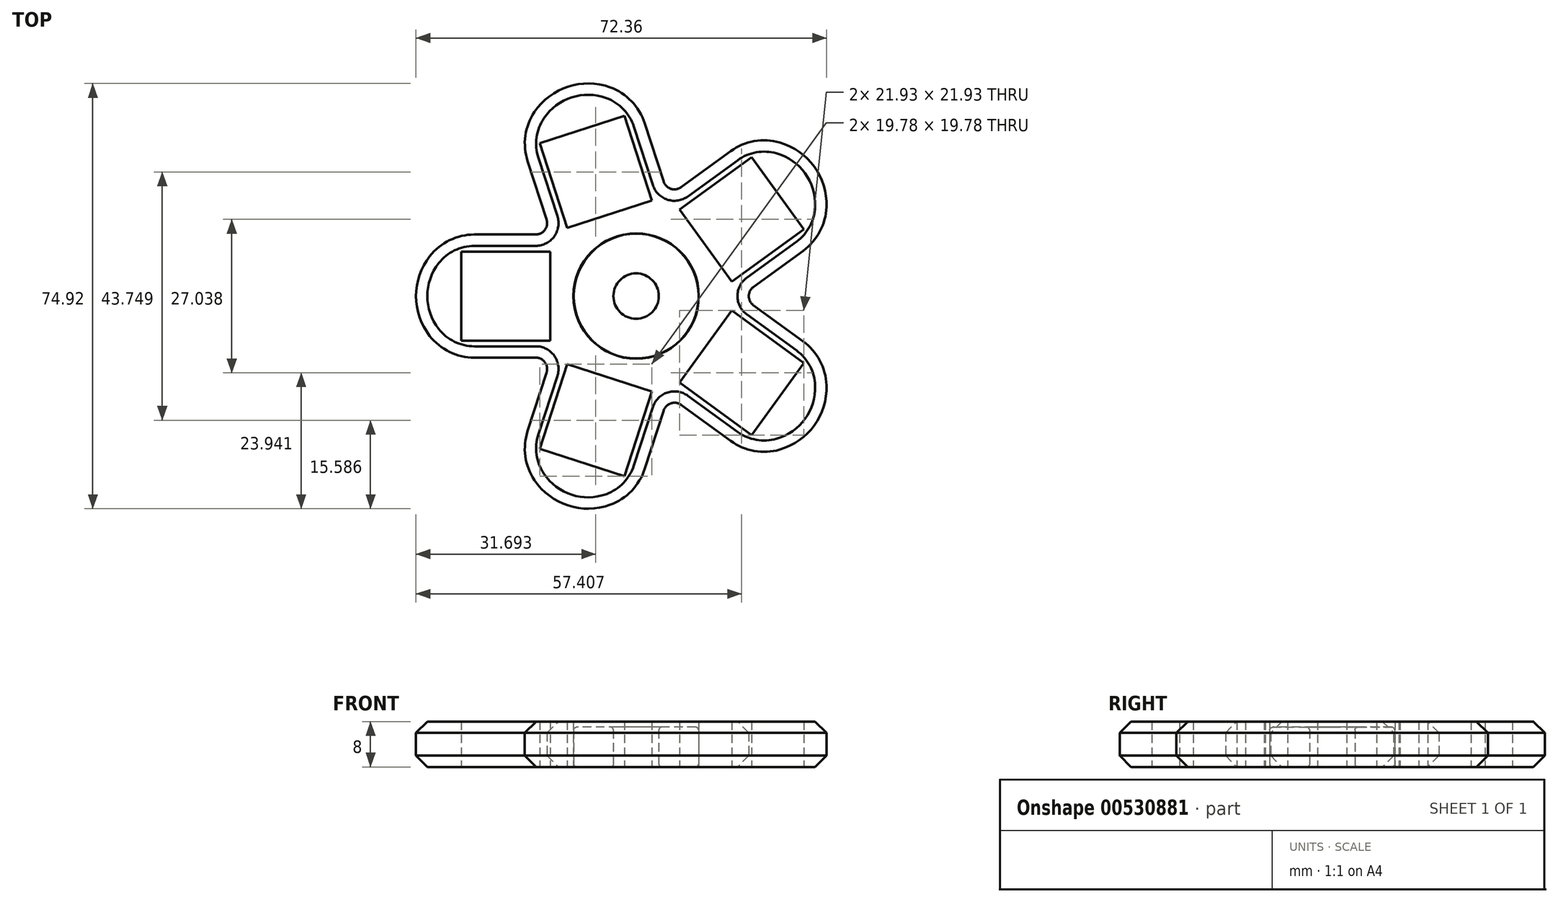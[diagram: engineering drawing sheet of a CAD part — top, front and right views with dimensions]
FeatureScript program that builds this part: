
annotation { "Feature Type Name" : "Feature", "Feature Type Description" : "" }
export const myFeature = defineFeature(function(context is Context, id is Id, definition is map)
    precondition{}
    {
        {
            var Q0;
            Q0=qCreatedBy(makeId("Top.planeOp"),FACE);
            var sketch = newSketch(context, id + "F0", { "sketchPlane" : qUnion([Q0])});
            skCircle(sketch, "E0", {"center": v(0, 0) * mm, "radius": 11 * mm});
            skCircle(sketch, "E1", {"center": v(0, 0) * mm, "radius": 4 * mm});
            skSolve(sketch);
        }
        {
            var Q0;
            Q0=makeQuery(id+"F0.imprint","IMPRINT",FACE,{"disambiguationData":[TD([[makeQuery(id+"F0.imprint","IMPRINT",EDGE,{"derivedFrom":sQuery(id+"F0.wireOp",EDGE,"E0")}),1.0]])]});
            extrude(context, id + "F1", {"entities" : qUnion([Q0]), "depth" : 7 * mm, "offsetDistance" : 25 * mm});
        }
        {
            var Q0;
            Q0=makeQuery(id+"F1.opExtrude","CAP_FACE",FACE,{"disambiguationData":[OSD([sQuery(id+"F0.wireOp",EDGE,"E0"),sQuery(id+"F0.wireOp",EDGE,"E1")])],"isStart":true});
            var sketch = newSketch(context, id + "F2", { "sketchPlane" : qUnion([Q0])});
            skCircle(sketch, "E2.0", {"center": v(0, 0) * mm, "radius": 11.05 * mm});
            skCircle(sketch, "E3.0", {"center": v(0, 0) * mm, "radius": 15.05 * mm});
            skLineSegment(sketch, "E4", {"start": v(0, 0) * mm, "end": v(-23, 0) * mm, "construction": true});
            skLineSegment(sketch, "E5.bottom", {"start": v(-30.85, -7.85) * mm, "end": v(-15.15, -7.85) * mm});
            skLineSegment(sketch, "E5.top", {"start": v(-30.85, 7.85) * mm, "end": v(-15.15, 7.85) * mm});
            skLineSegment(sketch, "E5.left", {"start": v(-30.85, -7.85) * mm, "end": v(-30.85, 7.85) * mm});
            skLineSegment(sketch, "E5.right", {"start": v(-15.15, -7.85) * mm, "end": v(-15.15, 7.85) * mm});
            skPoint(sketch, "E5.middle", {"position": v(-23, 0) * mm});
            skCircle(sketch, "E6", {"center": v(0, 0) * mm, "radius": 50 * mm, "construction": true});
            skLineSegment(sketch, "E7", {"start": v(-23, 0) * mm, "end": v(-38.8, 0) * mm, "construction": true});
            skLineSegment(sketch, "E8", {"start": v(-30.85, 7.85) * mm, "end": v(-30.85, 10.85) * mm, "construction": true});
            skLineSegment(sketch, "E9.0", {"start": v(-23, 10.85) * mm, "end": v(-30.85, 10.85) * mm});
            skLineSegment(sketch, "E9.1", {"start": v(0, 10.85) * mm, "end": v(-2.1, 10.85) * mm, "construction": true});
            skLineSegment(sketch, "E10.trimOffspring", {"start": v(-10.43, 10.85) * mm, "end": v(-23, 10.85) * mm});
            skLineSegment(sketch, "E11.MirrorCS", {"start": v(-10.43, -10.85) * mm, "end": v(-23, -10.85) * mm});
            skLineSegment(sketch, "E12.MirrorCS", {"start": v(-23, -10.85) * mm, "end": v(-30.85, -10.85) * mm});
            skArc(sketch, "E13", {"start": v(-30.85, 10.85) * mm, "mid": v(-38.8, 0) * mm, "end": v(-30.85, -10.85) * mm});
            skLineSegment(sketch, "E14.1.0", {"start": v(-2.07, -31.77) * mm, "end": v(2.78, -16.83) * mm});
            skLineSegment(sketch, "E14.1.1", {"start": v(2.78, -16.83) * mm, "end": v(-12.15, -11.98) * mm});
            skLineSegment(sketch, "E14.1.2", {"start": v(-17, -26.91) * mm, "end": v(-12.15, -11.98) * mm});
            skLineSegment(sketch, "E14.1.3", {"start": v(-13.54, -6.57) * mm, "end": v(-17.43, -18.52) * mm});
            skLineSegment(sketch, "E14.1.4", {"start": v(-17.43, -18.52) * mm, "end": v(-19.85, -25.99) * mm});
            skLineSegment(sketch, "E14.1.5", {"start": v(-2.07, -31.77) * mm, "end": v(-17, -26.91) * mm});
            skArc(sketch, "E14.1.6", {"start": v(-19.85, -25.99) * mm, "mid": v(-11.99, -36.9) * mm, "end": v(0.79, -32.7) * mm});
            skLineSegment(sketch, "E14.1.7", {"start": v(3.21, -25.23) * mm, "end": v(0.79, -32.7) * mm});
            skLineSegment(sketch, "E14.1.8", {"start": v(7.1, -13.27) * mm, "end": v(3.21, -25.23) * mm});
            skLineSegment(sketch, "E14.2.0", {"start": v(29.57, -11.78) * mm, "end": v(16.87, -2.55) * mm});
            skLineSegment(sketch, "E14.2.1", {"start": v(16.87, -2.55) * mm, "end": v(7.64, -15.26) * mm});
            skLineSegment(sketch, "E14.2.2", {"start": v(20.34, -24.48) * mm, "end": v(7.64, -15.26) * mm});
            skLineSegment(sketch, "E14.2.3", {"start": v(2.06, -14.9) * mm, "end": v(12.23, -22.3) * mm});
            skLineSegment(sketch, "E14.2.4", {"start": v(12.23, -22.3) * mm, "end": v(18.58, -26.91) * mm});
            skLineSegment(sketch, "E14.2.5", {"start": v(29.57, -11.78) * mm, "end": v(20.34, -24.48) * mm});
            skArc(sketch, "E14.2.6", {"start": v(18.58, -26.91) * mm, "mid": v(31.39, -22.8) * mm, "end": v(31.34, -9.36) * mm});
            skLineSegment(sketch, "E14.2.7", {"start": v(24.98, -4.74) * mm, "end": v(31.34, -9.36) * mm});
            skLineSegment(sketch, "E14.2.8", {"start": v(14.82, 2.65) * mm, "end": v(24.98, -4.74) * mm});
            skCircle(sketch, "E15", {"center": v(0, 0) * mm, "radius": 32.7 * mm, "construction": true});
            skLineSegment(sketch, "E16.3.3.0", {"start": v(7.64, 15.26) * mm, "end": v(16.87, 2.55) * mm});
            skLineSegment(sketch, "E16.6.3.0", {"start": v(29.57, 11.78) * mm, "end": v(16.87, 2.55) * mm});
            skLineSegment(sketch, "E16.9.3.0", {"start": v(14.82, -2.65) * mm, "end": v(24.98, 4.74) * mm});
            skLineSegment(sketch, "E16.12.3.0", {"start": v(24.98, 4.74) * mm, "end": v(31.34, 9.36) * mm});
            skLineSegment(sketch, "E16.15.3.0", {"start": v(20.34, 24.48) * mm, "end": v(29.57, 11.78) * mm});
            skArc(sketch, "E16.18.3.0", {"start": v(31.34, 9.36) * mm, "mid": v(31.39, 22.8) * mm, "end": v(18.58, 26.91) * mm});
            skLineSegment(sketch, "E16.21.3.0", {"start": v(20.34, 24.48) * mm, "end": v(7.64, 15.26) * mm});
            skLineSegment(sketch, "E16.22.3.0", {"start": v(12.23, 22.3) * mm, "end": v(18.58, 26.91) * mm});
            skLineSegment(sketch, "E16.25.3.0", {"start": v(2.06, 14.9) * mm, "end": v(12.23, 22.3) * mm});
            skLineSegment(sketch, "E16.3.4.0", {"start": v(-12.15, 11.98) * mm, "end": v(2.78, 16.83) * mm});
            skLineSegment(sketch, "E16.6.4.0", {"start": v(-2.07, 31.77) * mm, "end": v(2.78, 16.83) * mm});
            skLineSegment(sketch, "E16.9.4.0", {"start": v(7.1, 13.27) * mm, "end": v(3.21, 25.23) * mm});
            skLineSegment(sketch, "E16.12.4.0", {"start": v(3.21, 25.23) * mm, "end": v(0.79, 32.7) * mm});
            skLineSegment(sketch, "E16.15.4.0", {"start": v(-17, 26.91) * mm, "end": v(-2.07, 31.77) * mm});
            skArc(sketch, "E16.18.4.0", {"start": v(0.79, 32.7) * mm, "mid": v(-11.99, 36.9) * mm, "end": v(-19.85, 25.99) * mm});
            skLineSegment(sketch, "E16.21.4.0", {"start": v(-17, 26.91) * mm, "end": v(-12.15, 11.98) * mm});
            skLineSegment(sketch, "E16.22.4.0", {"start": v(-17.43, 18.52) * mm, "end": v(-19.85, 25.99) * mm});
            skLineSegment(sketch, "E16.25.4.0", {"start": v(-13.54, 6.57) * mm, "end": v(-17.43, 18.52) * mm});
            skSolve(sketch);
        }
        {
            var Q0;
            Q0=makeQuery(id+"F1.opExtrude","CAP_EDGE",EDGE,{"disambiguationData":[OSD([sQuery(id+"F0.wireOp",EDGE,"E0")])],"isStart":false});
            var Q1;
            Q1=makeQuery(id+"F1.opExtrude","CAP_EDGE",EDGE,{"disambiguationData":[OSD([sQuery(id+"F0.wireOp",EDGE,"E0")])],"isStart":true});
            var Q2;
            Q2=makeQuery(id+"F1.opExtrude","CAP_EDGE",EDGE,{"disambiguationData":[OSD([sQuery(id+"F0.wireOp",EDGE,"E1")])],"isStart":false});
            var Q3;
            Q3=makeQuery(id+"F1.opExtrude","CAP_EDGE",EDGE,{"disambiguationData":[OSD([sQuery(id+"F0.wireOp",EDGE,"E1")])],"isStart":true});
            fillet(context, id + "F3", {"entities" : qUnion([Q0, Q1, Q2, Q3]), "radius" : .5 * mm, "tangentPropagation" : true, "allowEdgeOverflow" : false});
        }
        {
            var Q0;
            {var subQ5=sQuery(id+"F2.wireOp",EDGE,"E14.2.0");Q0=makeQuery(id+"F2.imprint","IMPRINT",FACE,{"disambiguationData":[TD([[makeQuery(id+"F2.imprint","IMPRINT",EDGE,{"derivedFrom":subQ5}),-1.0]])]});}
            var Q1;
            {var subQ6=sQuery(id+"F2.wireOp",EDGE,"E14.1.0");Q1=makeQuery(id+"F2.imprint","IMPRINT",FACE,{"disambiguationData":[TD([[makeQuery(id+"F2.imprint","IMPRINT",EDGE,{"derivedFrom":subQ6}),-1.0]])]});}
            var Q2;
            {var subQ5=sQuery(id+"F2.wireOp",EDGE,"E5.bottom");Q2=makeQuery(id+"F2.imprint","IMPRINT",FACE,{"disambiguationData":[TD([[makeQuery(id+"F2.imprint","IMPRINT",EDGE,{"derivedFrom":subQ5}),-1.0]])]});}
            var Q3;
            Q3=makeQuery(id+"F2.imprint","IMPRINT",FACE,{"disambiguationData":[TD([[makeQuery(id+"F2.imprint","IMPRINT",EDGE,{"derivedFrom":sQuery(id+"F2.wireOp",EDGE,"E16.3.4.0")}),-1.0]])]});
            var Q4;
            {var subQ0=sQuery(id+"F2.wireOp",EDGE,"E10.trimOffspring");var subQ1=sQuery(id+"F2.wireOp",EDGE,"E3.0");var subQ2=makeQuery(id+"F2.imprint","INTERSECT",VERTEX,{"derivedFrom":[subQ1,subQ0]});Q4=makeQuery(id+"F2.imprint","IMPRINT",FACE,{"disambiguationData":[TD([[makeQuery(id+"F2.imprint","IMPRINT",EDGE,{"disambiguationData":[TD([[subQ2,-1.0]])],"derivedFrom":subQ1}),-1.0]])]});}
            var Q5;
            Q5=makeQuery(id+"F2.imprint","IMPRINT",FACE,{"disambiguationData":[TD([[makeQuery(id+"F2.imprint","IMPRINT",EDGE,{"derivedFrom":sQuery(id+"F2.wireOp",EDGE,"E16.3.3.0")}),-1.0]])]});
            var Q6;
            {var subQ0=sQuery(id+"F2.wireOp",EDGE,"E16.25.3.0");var subQ1=sQuery(id+"F2.wireOp",EDGE,"E3.0");var subQ2=makeQuery(id+"F2.imprint","INTERSECT",VERTEX,{"derivedFrom":[subQ1,subQ0]});Q6=makeQuery(id+"F2.imprint","IMPRINT",FACE,{"disambiguationData":[TD([[makeQuery(id+"F2.imprint","IMPRINT",EDGE,{"disambiguationData":[TD([[subQ2,1.0]])],"derivedFrom":subQ1}),-1.0]])]});}
            var Q7;
            {var subQ0=sQuery(id+"F2.wireOp",EDGE,"E14.2.8");var subQ1=sQuery(id+"F2.wireOp",EDGE,"E3.0");var subQ2=makeQuery(id+"F2.imprint","INTERSECT",VERTEX,{"derivedFrom":[subQ1,subQ0]});Q7=makeQuery(id+"F2.imprint","IMPRINT",FACE,{"disambiguationData":[TD([[makeQuery(id+"F2.imprint","IMPRINT",EDGE,{"disambiguationData":[TD([[subQ2,1.0]])],"derivedFrom":subQ1}),-1.0]])]});}
            var Q8;
            {var subQ0=sQuery(id+"F2.wireOp",EDGE,"E11.MirrorCS");var subQ1=sQuery(id+"F2.wireOp",EDGE,"E3.0");var subQ2=makeQuery(id+"F2.imprint","INTERSECT",VERTEX,{"derivedFrom":[subQ1,subQ0]});Q8=makeQuery(id+"F2.imprint","IMPRINT",FACE,{"disambiguationData":[TD([[makeQuery(id+"F2.imprint","IMPRINT",EDGE,{"disambiguationData":[TD([[subQ2,1.0]])],"derivedFrom":subQ1}),-1.0]])]});}
            var Q9;
            Q9=makeQuery(id+"F2.imprint","IMPRINT",FACE,{"disambiguationData":[TD([[makeQuery(id+"F2.imprint","IMPRINT",EDGE,{"derivedFrom":sQuery(id+"F2.wireOp",EDGE,"E2.0")}),-1.0]])]});
            var Q10;
            {var subQ0=sQuery(id+"F2.wireOp",EDGE,"E14.1.8");var subQ1=sQuery(id+"F2.wireOp",EDGE,"E3.0");var subQ2=makeQuery(id+"F2.imprint","INTERSECT",VERTEX,{"derivedFrom":[subQ1,subQ0]});Q10=makeQuery(id+"F2.imprint","IMPRINT",FACE,{"disambiguationData":[TD([[makeQuery(id+"F2.imprint","IMPRINT",EDGE,{"disambiguationData":[TD([[subQ2,1.0]])],"derivedFrom":subQ1}),-1.0]])]});}
            extrude(context, id + "F4", {"entities" : qUnion([Q0, Q1, Q2, Q3, Q4, Q5, Q6, Q7, Q8, Q9, Q10]), "oppositeDirection" : true, "depth" : 8 * mm, "offsetDistance" : 25 * mm});
        }
        {
            var Q0;
            Q0=makeQuery(id+"F4.opExtrude","SWEPT_EDGE",EDGE,{"disambiguationData":[OSD([sQuery(id+"F2.wireOp",EDGE,"E3.0"),sQuery(id+"F2.wireOp",EDGE,"E14.2.3")])]});
            var Q1;
            Q1=makeQuery(id+"F4.opExtrude","SWEPT_EDGE",EDGE,{"disambiguationData":[OSD([sQuery(id+"F2.wireOp",EDGE,"E3.0"),sQuery(id+"F2.wireOp",EDGE,"E14.1.8")])]});
            var Q2;
            Q2=makeQuery(id+"F4.opExtrude","SWEPT_EDGE",EDGE,{"disambiguationData":[OSD([sQuery(id+"F2.wireOp",EDGE,"E3.0"),sQuery(id+"F2.wireOp",EDGE,"E14.2.8")])]});
            var Q3;
            Q3=makeQuery(id+"F4.opExtrude","SWEPT_EDGE",EDGE,{"disambiguationData":[OSD([sQuery(id+"F2.wireOp",EDGE,"E3.0"),sQuery(id+"F2.wireOp",EDGE,"E10.trimOffspring")])]});
            var Q4;
            Q4=makeQuery(id+"F4.opExtrude","SWEPT_EDGE",EDGE,{"disambiguationData":[OSD([sQuery(id+"F2.wireOp",EDGE,"E3.0"),sQuery(id+"F2.wireOp",EDGE,"E11.MirrorCS")])]});
            var Q5;
            Q5=makeQuery(id+"F4.opExtrude","SWEPT_EDGE",EDGE,{"disambiguationData":[OSD([sQuery(id+"F2.wireOp",EDGE,"E3.0"),sQuery(id+"F2.wireOp",EDGE,"E14.1.3")])]});
            var Q6;
            Q6=makeQuery(id+"F4.opExtrude","SWEPT_EDGE",EDGE,{"disambiguationData":[OSD([sQuery(id+"F2.wireOp",EDGE,"E16.25.3.0"),sQuery(id+"F2.wireOp",EDGE,"E16.9.4.0")])]});
            fillet(context, id + "F5", {"entities" : qUnion([Q0, Q1, Q2, Q3, Q4, Q5, Q6]), "radius" : 2 * mm, "tangentPropagation" : true, "allowEdgeOverflow" : false});
        }
        {
            var Q0;
            Q0=makeQuery(id+"F4.opExtrude","SWEPT_EDGE",EDGE,{"disambiguationData":[OSD([sQuery(id+"F2.wireOp",EDGE,"E14.2.4"),sQuery(id+"F2.wireOp",EDGE,"E14.2.6")])]});
            var Q1;
            Q1=makeQuery(id+"F4.opExtrude","SWEPT_EDGE",EDGE,{"disambiguationData":[OSD([sQuery(id+"F2.wireOp",EDGE,"E14.2.6"),sQuery(id+"F2.wireOp",EDGE,"E14.2.7")])]});
            var Q2;
            Q2=makeQuery(id+"F4.opExtrude","SWEPT_EDGE",EDGE,{"disambiguationData":[OSD([sQuery(id+"F2.wireOp",EDGE,"E9.0"),sQuery(id+"F2.wireOp",EDGE,"E13")])]});
            var Q3;
            Q3=makeQuery(id+"F4.opExtrude","SWEPT_EDGE",EDGE,{"disambiguationData":[OSD([sQuery(id+"F2.wireOp",EDGE,"E12.MirrorCS"),sQuery(id+"F2.wireOp",EDGE,"E13")])]});
            var Q4;
            Q4=makeQuery(id+"F4.opExtrude","SWEPT_EDGE",EDGE,{"disambiguationData":[OSD([sQuery(id+"F2.wireOp",EDGE,"E14.1.4"),sQuery(id+"F2.wireOp",EDGE,"E14.1.6")])]});
            var Q5;
            Q5=makeQuery(id+"F4.opExtrude","SWEPT_EDGE",EDGE,{"disambiguationData":[OSD([sQuery(id+"F2.wireOp",EDGE,"E14.1.6"),sQuery(id+"F2.wireOp",EDGE,"E14.1.7")])]});
            var Q6;
            Q6=makeQuery(id+"F4.opExtrude","SWEPT_EDGE",EDGE,{"disambiguationData":[OSD([sQuery(id+"F2.wireOp",EDGE,"E16.18.4.0"),sQuery(id+"F2.wireOp",EDGE,"E16.22.4.0")])]});
            var Q7;
            Q7=makeQuery(id+"F4.opExtrude","SWEPT_EDGE",EDGE,{"disambiguationData":[OSD([sQuery(id+"F2.wireOp",EDGE,"E16.12.4.0"),sQuery(id+"F2.wireOp",EDGE,"E16.18.4.0")])]});
            var Q8;
            Q8=makeQuery(id+"F4.opExtrude","SWEPT_EDGE",EDGE,{"disambiguationData":[OSD([sQuery(id+"F2.wireOp",EDGE,"E16.18.3.0"),sQuery(id+"F2.wireOp",EDGE,"E16.22.3.0")])]});
            var Q9;
            Q9=makeQuery(id+"F4.opExtrude","SWEPT_EDGE",EDGE,{"disambiguationData":[OSD([sQuery(id+"F2.wireOp",EDGE,"E16.12.3.0"),sQuery(id+"F2.wireOp",EDGE,"E16.18.3.0")])]});
            fillet(context, id + "F6", {"entities" : qUnion([Q0, Q1, Q2, Q3, Q4, Q5, Q6, Q7, Q8, Q9]), "radius" : 10 * mm, "tangentPropagation" : true, "allowEdgeOverflow" : false});
        }
        {
            var Q0;
            Q0=makeQuery(id+"F4.opExtrude","CAP_EDGE",EDGE,{"disambiguationData":[OSD([sQuery(id+"F2.wireOp",EDGE,"E14.2.6")])],"isStart":false});
            var Q1;
            Q1=makeQuery(id+"F4.opExtrude","CAP_EDGE",EDGE,{"disambiguationData":[OSD([sQuery(id+"F2.wireOp",EDGE,"E14.1.6")])],"isStart":false});
            var Q2;
            {var subQ0=sQuery(id+"F2.wireOp",EDGE,"E13");var subQ1=sQuery(id+"F2.wireOp",EDGE,"E9.0");Q2=makeQuery(id+"F6.opFillet","BLEND_EDGE",EDGE,{"blendedFrom":[makeQuery(id+"F4.opExtrude","SWEPT_EDGE",EDGE,{"disambiguationData":[OSD([subQ1,subQ0])]}),makeQuery(id+"F4.opExtrude","CAP_FACE",FACE,{"disambiguationData":[OSD([sQuery(id+"F2.wireOp",EDGE,"E2.0"),sQuery(id+"F2.wireOp",EDGE,"E3.0"),sQuery(id+"F2.wireOp",EDGE,"E5.bottom"),sQuery(id+"F2.wireOp",EDGE,"E5.top"),sQuery(id+"F2.wireOp",EDGE,"E5.left"),sQuery(id+"F2.wireOp",EDGE,"E5.right"),subQ1,sQuery(id+"F2.wireOp",EDGE,"E10.trimOffspring"),sQuery(id+"F2.wireOp",EDGE,"E11.MirrorCS"),sQuery(id+"F2.wireOp",EDGE,"E12.MirrorCS"),subQ0,sQuery(id+"F2.wireOp",EDGE,"E14.1.0"),sQuery(id+"F2.wireOp",EDGE,"E14.1.1"),sQuery(id+"F2.wireOp",EDGE,"E14.1.2"),sQuery(id+"F2.wireOp",EDGE,"E14.1.3"),sQuery(id+"F2.wireOp",EDGE,"E14.1.4"),sQuery(id+"F2.wireOp",EDGE,"E14.1.5"),sQuery(id+"F2.wireOp",EDGE,"E14.1.6"),sQuery(id+"F2.wireOp",EDGE,"E14.1.7"),sQuery(id+"F2.wireOp",EDGE,"E14.1.8"),sQuery(id+"F2.wireOp",EDGE,"E14.2.0"),sQuery(id+"F2.wireOp",EDGE,"E14.2.1"),sQuery(id+"F2.wireOp",EDGE,"E14.2.2"),sQuery(id+"F2.wireOp",EDGE,"E14.2.3"),sQuery(id+"F2.wireOp",EDGE,"E14.2.4"),sQuery(id+"F2.wireOp",EDGE,"E14.2.5"),sQuery(id+"F2.wireOp",EDGE,"E14.2.6"),sQuery(id+"F2.wireOp",EDGE,"E14.2.7"),sQuery(id+"F2.wireOp",EDGE,"E14.2.8")])],"isStart":false})],"blendedInto":[makeQuery(id+"F4.opExtrude","CAP_FACE",FACE,{"disambiguationData":[OSD([sQuery(id+"F2.wireOp",EDGE,"E2.0"),sQuery(id+"F2.wireOp",EDGE,"E3.0"),sQuery(id+"F2.wireOp",EDGE,"E5.bottom"),sQuery(id+"F2.wireOp",EDGE,"E5.top"),sQuery(id+"F2.wireOp",EDGE,"E5.left"),sQuery(id+"F2.wireOp",EDGE,"E5.right"),subQ1,sQuery(id+"F2.wireOp",EDGE,"E10.trimOffspring"),sQuery(id+"F2.wireOp",EDGE,"E11.MirrorCS"),sQuery(id+"F2.wireOp",EDGE,"E12.MirrorCS"),subQ0,sQuery(id+"F2.wireOp",EDGE,"E14.1.0"),sQuery(id+"F2.wireOp",EDGE,"E14.1.1"),sQuery(id+"F2.wireOp",EDGE,"E14.1.2"),sQuery(id+"F2.wireOp",EDGE,"E14.1.3"),sQuery(id+"F2.wireOp",EDGE,"E14.1.4"),sQuery(id+"F2.wireOp",EDGE,"E14.1.5"),sQuery(id+"F2.wireOp",EDGE,"E14.1.6"),sQuery(id+"F2.wireOp",EDGE,"E14.1.7"),sQuery(id+"F2.wireOp",EDGE,"E14.1.8"),sQuery(id+"F2.wireOp",EDGE,"E14.2.0"),sQuery(id+"F2.wireOp",EDGE,"E14.2.1"),sQuery(id+"F2.wireOp",EDGE,"E14.2.2"),sQuery(id+"F2.wireOp",EDGE,"E14.2.3"),sQuery(id+"F2.wireOp",EDGE,"E14.2.4"),sQuery(id+"F2.wireOp",EDGE,"E14.2.5"),sQuery(id+"F2.wireOp",EDGE,"E14.2.6"),sQuery(id+"F2.wireOp",EDGE,"E14.2.7"),sQuery(id+"F2.wireOp",EDGE,"E14.2.8")])],"isStart":false})]});}
            var Q3;
            Q3=makeQuery(id+"F4.opExtrude","CAP_EDGE",EDGE,{"disambiguationData":[OSD([sQuery(id+"F2.wireOp",EDGE,"E14.2.6")])],"isStart":true});
            var Q4;
            Q4=makeQuery(id+"F4.opExtrude","CAP_EDGE",EDGE,{"disambiguationData":[OSD([sQuery(id+"F2.wireOp",EDGE,"E13")])],"isStart":true});
            var Q5;
            Q5=makeQuery(id+"F4.opExtrude","CAP_EDGE",EDGE,{"disambiguationData":[OSD([sQuery(id+"F2.wireOp",EDGE,"E14.1.6")])],"isStart":true});
            chamfer(context, id + "F7", {"entities" : qUnion([Q0, Q1, Q2, Q3, Q4, Q5]), "width" : 2 * mm, "tangentPropagation" : true});
        }
    });
